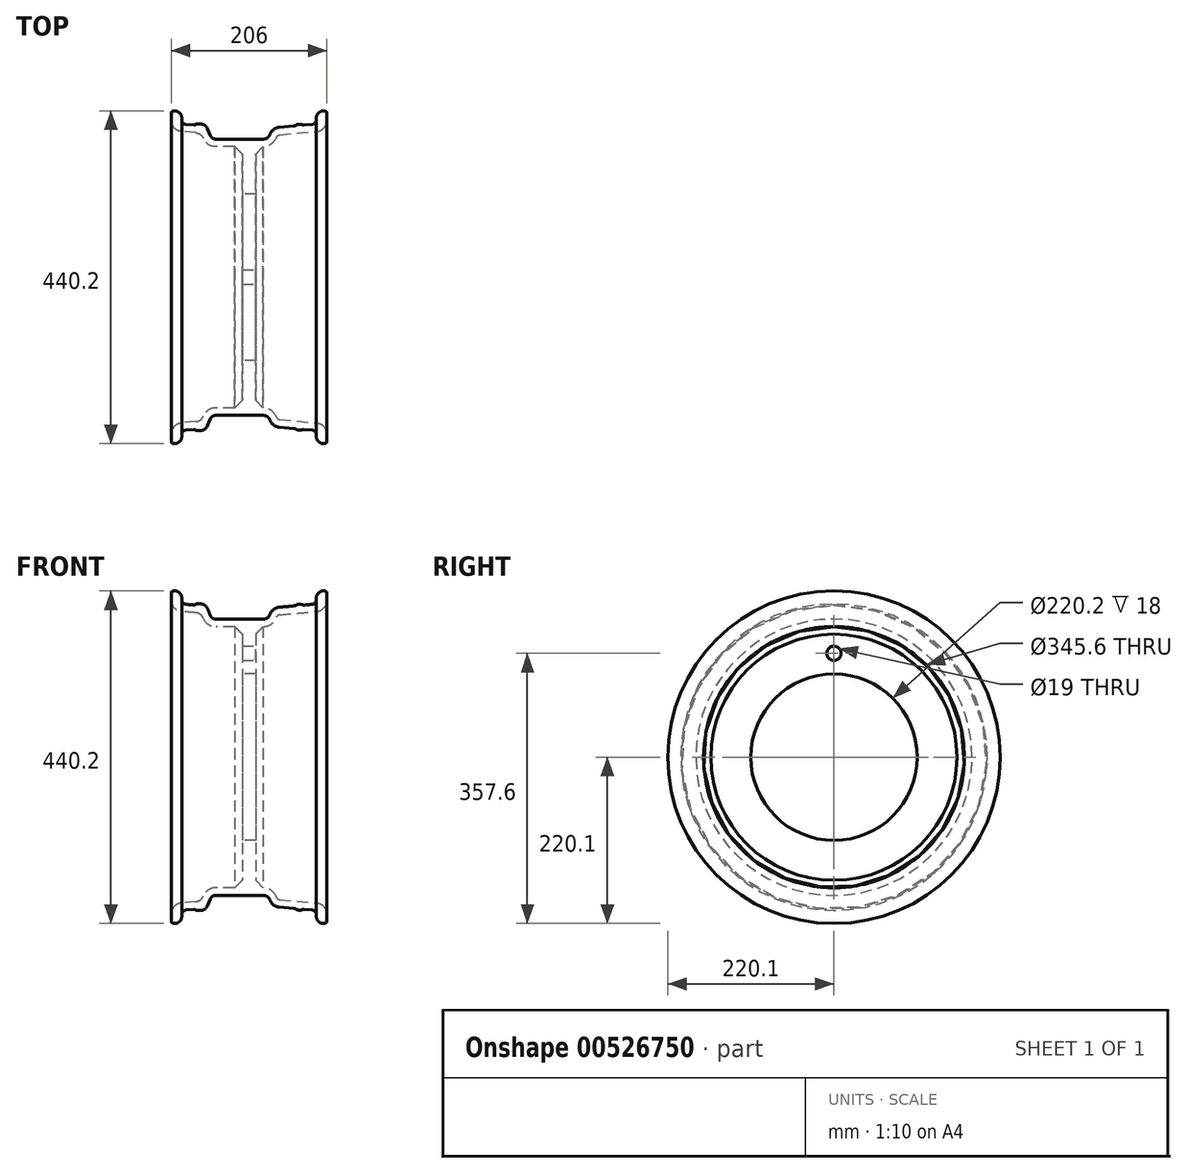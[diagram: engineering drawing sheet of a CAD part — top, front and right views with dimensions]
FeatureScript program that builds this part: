
annotation { "Feature Type Name" : "Feature", "Feature Type Description" : "" }
export const myFeature = defineFeature(function(context is Context, id is Id, definition is map)
    precondition{}
    {
        {
            var Q0;
            Q0=qCreatedBy(makeId("Top.planeOp"),FACE);
            var sketch = newSketch(context, id + "F0", { "sketchPlane" : qUnion([Q0])});
            skLineSegment(sketch, "E0", {"start": v(-9.12, 160) * mm, "end": v(-9.12, 172.8) * mm});
            skLineSegment(sketch, "E1", {"start": v(-9.12, 172.8) * mm, "end": v(8.88, 172.8) * mm});
            skLineSegment(sketch, "E2", {"start": v(8.88, 172.8) * mm, "end": v(8.88, 160) * mm});
            skLineSegment(sketch, "E3", {"start": v(8.88, 160) * mm, "end": v(8.88, 110.1) * mm});
            skLineSegment(sketch, "E4", {"start": v(-9.12, 160) * mm, "end": v(-9.12, 110.1) * mm});
            skArc(sketch, "E5", {"start": v(-73.15, 201.4) * mm, "mid": v(-71.83, 201.59) * mm, "end": v(-70.71, 202.33) * mm});
            skLineSegment(sketch, "E6", {"start": v(-83.65, 202.32) * mm, "end": v(-73.15, 201.4) * mm});
            skArc(sketch, "E7", {"start": v(-89.12, 208.3) * mm, "mid": v(-87.55, 204.25) * mm, "end": v(-83.65, 202.32) * mm});
            skArc(sketch, "E8", {"start": v(-89.12, 210.4) * mm, "mid": v(-91.97, 217.26) * mm, "end": v(-98.82, 220.1) * mm});
            skArc(sketch, "E9", {"start": v(-98.82, 220.1) * mm, "mid": v(-100.74, 219.8) * mm, "end": v(-102.48, 218.95) * mm});
            skArc(sketch, "E10", {"start": v(-102.48, 218.95) * mm, "mid": v(-102.95, 218.42) * mm, "end": v(-103.12, 217.72) * mm});
            skArc(sketch, "E11", {"start": v(-103.12, 207.73) * mm, "mid": v(-99.18, 197.6) * mm, "end": v(-89.43, 192.8) * mm});
            skLineSegment(sketch, "E12", {"start": v(-51.54, 187.8) * mm, "end": v(-55.15, 196.73) * mm});
            skArc(sketch, "E13", {"start": v(-55.15, 196.73) * mm, "mid": v(-58.72, 201.14) * mm, "end": v(-64.14, 202.8) * mm});
            skArc(sketch, "E14", {"start": v(-60.81, 184.06) * mm, "mid": v(-64.6, 188.94) * mm, "end": v(-70.36, 191.12) * mm});
            skArc(sketch, "E15", {"start": v(-60.81, 184.06) * mm, "mid": v(-54.19, 175.88) * mm, "end": v(-44.12, 172.8) * mm});
            skArc(sketch, "E16", {"start": v(-51.54, 187.8) * mm, "mid": v(-48.6, 184.17) * mm, "end": v(-44.12, 182.8) * mm});
            skLineSegment(sketch, "E17", {"start": v(-69.62, 202.8) * mm, "end": v(-64.14, 202.8) * mm});
            skArc(sketch, "E18", {"start": v(-69.62, 202.8) * mm, "mid": v(-70.22, 202.68) * mm, "end": v(-70.71, 202.33) * mm});
            skArc(sketch, "E19", {"start": v(98.58, 220.1) * mm, "mid": v(91.72, 217.26) * mm, "end": v(88.88, 210.4) * mm});
            skArc(sketch, "E20", {"start": v(83.4, 202.32) * mm, "mid": v(87.3, 204.25) * mm, "end": v(88.88, 208.3) * mm});
            skLineSegment(sketch, "E21", {"start": v(73.12, 201.42) * mm, "end": v(83.4, 202.32) * mm});
            skArc(sketch, "E22", {"start": v(70.37, 201.83) * mm, "mid": v(71.72, 201.46) * mm, "end": v(73.12, 201.42) * mm});
            skArc(sketch, "E23", {"start": v(70.37, 201.83) * mm, "mid": v(66.06, 202.47) * mm, "end": v(61.92, 201.1) * mm});
            skArc(sketch, "E24", {"start": v(59.29, 200.21) * mm, "mid": v(60.66, 200.5) * mm, "end": v(61.92, 201.1) * mm});
            skLineSegment(sketch, "E25", {"start": v(40.12, 198.54) * mm, "end": v(59.29, 200.21) * mm});
            skArc(sketch, "E26", {"start": v(40.12, 198.54) * mm, "mid": v(32.3, 195.5) * mm, "end": v(27.33, 188.72) * mm});
            skLineSegment(sketch, "E27", {"start": v(-89.43, 192.8) * mm, "end": v(-70.36, 191.12) * mm});
            skLineSegment(sketch, "E28", {"start": v(-44.12, 172.8) * mm, "end": v(18.34, 172.8) * mm});
            skArc(sketch, "E29", {"start": v(18.34, 172.8) * mm, "mid": v(29.22, 176.22) * mm, "end": v(36.18, 185.26) * mm});
            skArc(sketch, "E30", {"start": v(40.44, 188.53) * mm, "mid": v(37.84, 187.52) * mm, "end": v(36.18, 185.26) * mm});
            skLineSegment(sketch, "E31", {"start": v(89.18, 192.8) * mm, "end": v(40.44, 188.53) * mm});
            skArc(sketch, "E32", {"start": v(89.18, 192.8) * mm, "mid": v(98.93, 197.6) * mm, "end": v(102.88, 207.73) * mm});
            skArc(sketch, "E33", {"start": v(102.88, 217.72) * mm, "mid": v(102.7, 218.42) * mm, "end": v(102.23, 218.95) * mm});
            skArc(sketch, "E34", {"start": v(102.23, 218.95) * mm, "mid": v(100.5, 219.8) * mm, "end": v(98.58, 220.1) * mm});
            skArc(sketch, "E35", {"start": v(18.88, 182.8) * mm, "mid": v(24.04, 184.43) * mm, "end": v(27.33, 188.72) * mm});
            skLineSegment(sketch, "E36", {"start": v(-44.12, 182.8) * mm, "end": v(18.88, 182.8) * mm});
            skLineSegment(sketch, "E37", {"start": v(102.88, 217.72) * mm, "end": v(102.88, 207.73) * mm});
            skLineSegment(sketch, "E38", {"start": v(88.88, 208.3) * mm, "end": v(88.88, 210.4) * mm});
            skLineSegment(sketch, "E39", {"start": v(-103.12, 207.73) * mm, "end": v(-103.12, 217.72) * mm});
            skLineSegment(sketch, "E40", {"start": v(-89.12, 210.4) * mm, "end": v(-89.12, 208.3) * mm});
            skLineSegment(sketch, "E41", {"start": v(-9.12, 162.8) * mm, "end": v(-19.12, 172.8) * mm});
            skLineSegment(sketch, "E42", {"start": v(8.88, 162.8) * mm, "end": v(18.34, 172.8) * mm});
            skLineSegment(sketch, "E43", {"start": v(-9.12, 110.1) * mm, "end": v(8.88, 110.1) * mm});
            skLineSegment(sketch, "E44", {"start": v(-59.12, 0) * mm, "end": v(58.88, 0) * mm});
            skPoint(sketch, "E45", {"position": v(-0.12, 0) * mm});
            skSolve(sketch);
        }
        {
            var Q0;
            Q0 = qSketchRegion(id + "F0", true);
            var Q1;
            Q1=sQuery(id+"F0.wireOp",EDGE,"E44");
            revolve(context, id + "F1", {"entities" : qUnion([Q0]), "axis" : qUnion([Q1]), "revolveType" : RevolveType.FULL});
        }
        {
            var Q0;
            Q0=makeQuery(id+"F1.opRevolve","SWEPT_FACE",FACE,{"disambiguationData":[OSD([sQuery(id+"F0.wireOp",EDGE,"E2"),sQuery(id+"F0.wireOp",EDGE,"E3")])]});
            var sketch = newSketch(context, id + "F2", { "sketchPlane" : qUnion([Q0])});
            skCircle(sketch, "E46", {"center": v(0, 0) * mm, "radius": 137.5 * mm, "construction": true});
            skLineSegment(sketch, "E47", {"start": v(0, 0) * mm, "end": v(0, 137.5) * mm, "construction": true});
            skPoint(sketch, "E48", {"position": v(0, 137.5) * mm});
            skSolve(sketch);
        }
        {
            var Q0;
            Q0=sQuery(id+"F2.wireOp",VERTEX,"E48");
            var Q1;
            Q1=makeQuery(id+"F1.opRevolve","SWEPT_BODY",BODY,{"disambiguationData":[OSD([sQuery(id+"F0.wireOp",EDGE,"E0"),sQuery(id+"F0.wireOp",EDGE,"E2"),sQuery(id+"F0.wireOp",EDGE,"E3"),sQuery(id+"F0.wireOp",EDGE,"E4"),sQuery(id+"F0.wireOp",EDGE,"E5"),sQuery(id+"F0.wireOp",EDGE,"E6"),sQuery(id+"F0.wireOp",EDGE,"E7"),sQuery(id+"F0.wireOp",EDGE,"E8"),sQuery(id+"F0.wireOp",EDGE,"E9"),sQuery(id+"F0.wireOp",EDGE,"E10"),sQuery(id+"F0.wireOp",EDGE,"E11"),sQuery(id+"F0.wireOp",EDGE,"E12"),sQuery(id+"F0.wireOp",EDGE,"E13"),sQuery(id+"F0.wireOp",EDGE,"E14"),sQuery(id+"F0.wireOp",EDGE,"E15"),sQuery(id+"F0.wireOp",EDGE,"E16"),sQuery(id+"F0.wireOp",EDGE,"E17"),sQuery(id+"F0.wireOp",EDGE,"E18"),sQuery(id+"F0.wireOp",EDGE,"E19"),sQuery(id+"F0.wireOp",EDGE,"E20"),sQuery(id+"F0.wireOp",EDGE,"E21"),sQuery(id+"F0.wireOp",EDGE,"E22"),sQuery(id+"F0.wireOp",EDGE,"E23"),sQuery(id+"F0.wireOp",EDGE,"E24"),sQuery(id+"F0.wireOp",EDGE,"E25"),sQuery(id+"F0.wireOp",EDGE,"E26"),sQuery(id+"F0.wireOp",EDGE,"E27"),sQuery(id+"F0.wireOp",EDGE,"E28"),sQuery(id+"F0.wireOp",EDGE,"E29"),sQuery(id+"F0.wireOp",EDGE,"E30"),sQuery(id+"F0.wireOp",EDGE,"E31"),sQuery(id+"F0.wireOp",EDGE,"E32"),sQuery(id+"F0.wireOp",EDGE,"E33"),sQuery(id+"F0.wireOp",EDGE,"E34"),sQuery(id+"F0.wireOp",EDGE,"E35"),sQuery(id+"F0.wireOp",EDGE,"E36"),sQuery(id+"F0.wireOp",EDGE,"E37"),sQuery(id+"F0.wireOp",EDGE,"E38"),sQuery(id+"F0.wireOp",EDGE,"E39"),sQuery(id+"F0.wireOp",EDGE,"E40"),sQuery(id+"F0.wireOp",EDGE,"E42"),sQuery(id+"F0.wireOp",EDGE,"E41"),sQuery(id+"F0.wireOp",EDGE,"E43")])]});
            hole(context, id + "F3", {"style" : HoleStyle.SIMPLE, "endStyle" : HoleEndStyle.THROUGH, "holeDiameter" : 19 * mm, "isTappedThrough" : true, "tappedDepth" : 12 * mm, "tapClearance" : 3, "startFromSketch" : true, "locations" : qUnion([Q0]), "scope" : qUnion([Q1])});
        }
    });
